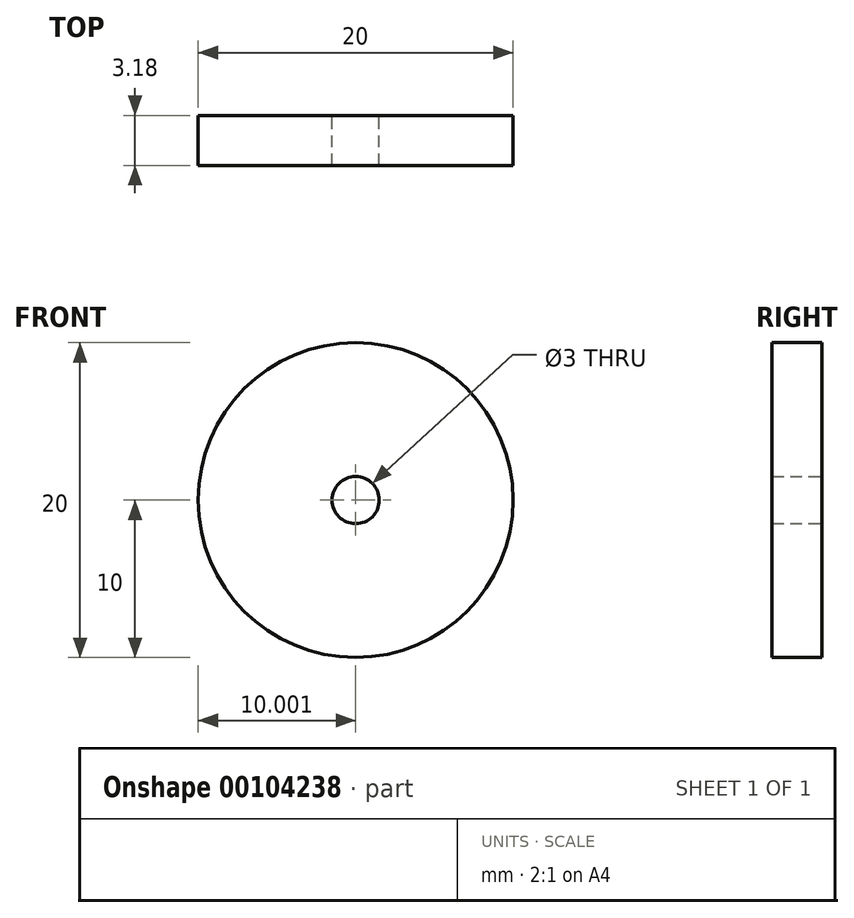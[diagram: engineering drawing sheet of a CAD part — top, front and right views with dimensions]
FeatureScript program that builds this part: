
annotation { "Feature Type Name" : "Feature", "Feature Type Description" : "" }
export const myFeature = defineFeature(function(context is Context, id is Id, definition is map)
    precondition{}
    {
        {
            var Q0;
            Q0=qCreatedBy(makeId("Front.planeOp"),FACE);
            var sketch = newSketch(context, id + "F0", { "sketchPlane" : qUnion([Q0])});
            skCircle(sketch, "E0", {"center": v(-9.3, 26.08) * mm, "radius": 10 * mm});
            skCircle(sketch, "E1", {"center": v(-9.3, 26.08) * mm, "radius": 1.5 * mm});
            skSolve(sketch);
        }
        {
            var Q0;
            Q0=makeQuery(id+"F0.imprint","IMPRINT",FACE,{"disambiguationData":[TD([[makeQuery(id+"F0.imprint","IMPRINT",EDGE,{"derivedFrom":sQuery(id+"F0.wireOp",EDGE,"E0")}),1.0]])]});
            extrude(context, id + "F1", {"entities" : qUnion([Q0]), "depth" : 3.17 * mm});
        }
    });
